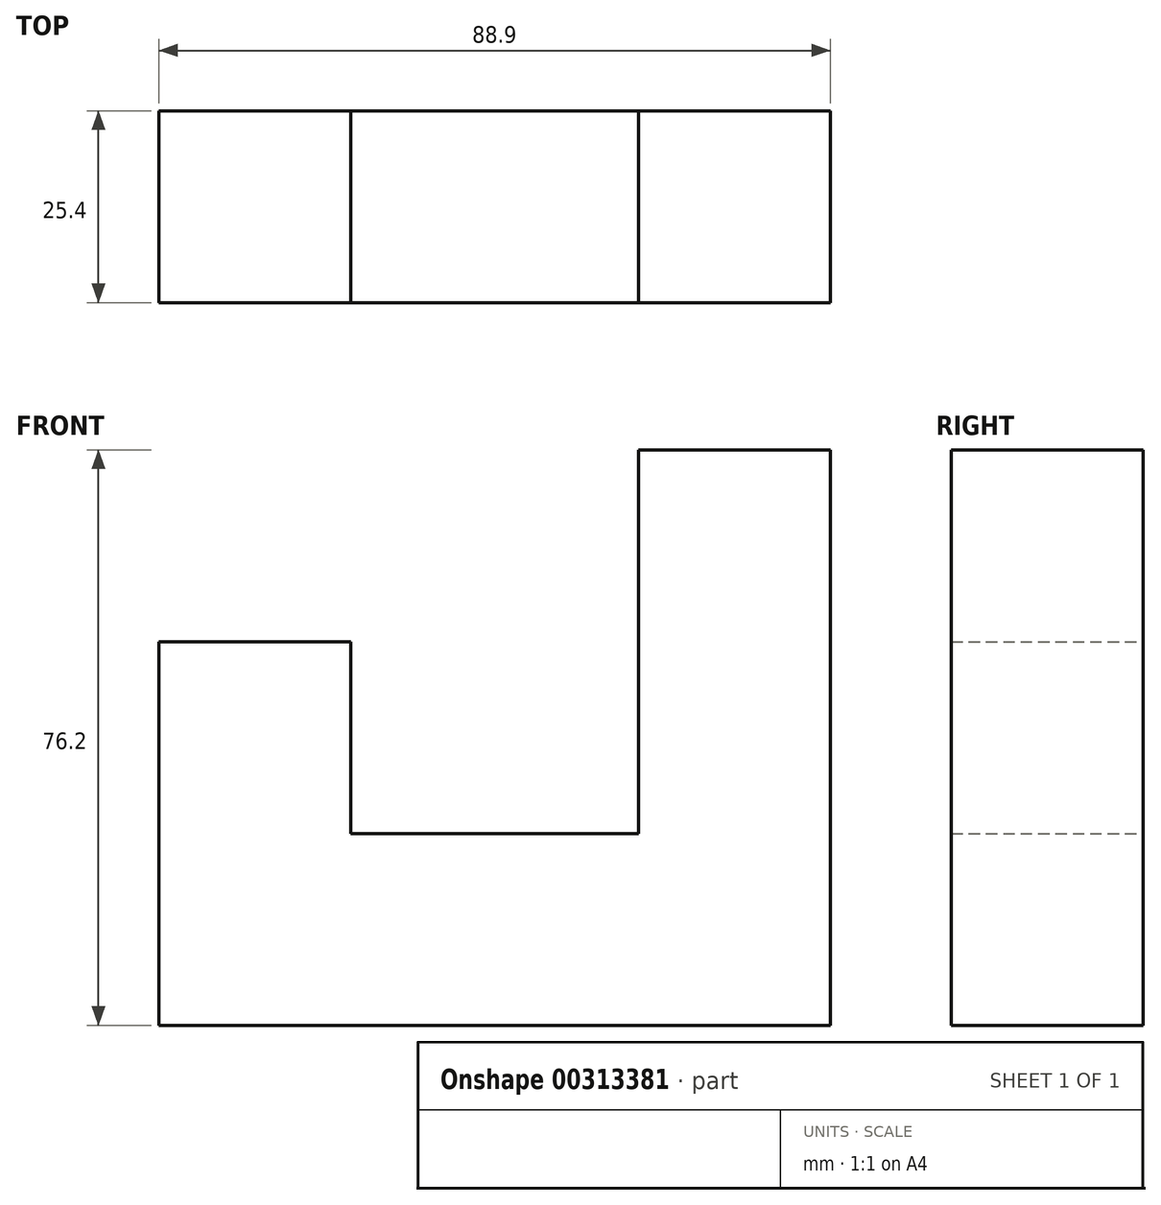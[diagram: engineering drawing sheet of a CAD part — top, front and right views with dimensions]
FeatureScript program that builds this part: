
annotation { "Feature Type Name" : "Feature", "Feature Type Description" : "" }
export const myFeature = defineFeature(function(context is Context, id is Id, definition is map)
    precondition{}
    {
        {
            var Q0;
            Q0=qCreatedBy(makeId("Front.planeOp"),FACE);
            var sketch = newSketch(context, id + "F0", { "sketchPlane" : qUnion([Q0])});
            skLineSegment(sketch, "E0", {"start": v(-43.6, -19.4) * mm, "end": v(45.3, -19.4) * mm});
            skLineSegment(sketch, "E1", {"start": v(45.3, -19.4) * mm, "end": v(45.3, 56.8) * mm});
            skLineSegment(sketch, "E2", {"start": v(45.3, 56.8) * mm, "end": v(19.9, 56.8) * mm});
            skLineSegment(sketch, "E3", {"start": v(19.9, 56.8) * mm, "end": v(19.9, 6) * mm});
            skLineSegment(sketch, "E4", {"start": v(19.9, 6) * mm, "end": v(-18.2, 6) * mm});
            skLineSegment(sketch, "E5", {"start": v(-18.2, 6) * mm, "end": v(-18.2, 31.4) * mm});
            skLineSegment(sketch, "E6", {"start": v(-18.2, 31.4) * mm, "end": v(-43.6, 31.4) * mm});
            skLineSegment(sketch, "E7", {"start": v(-43.6, 31.4) * mm, "end": v(-43.6, -19.4) * mm});
            skSolve(sketch);
        }
        {
            var Q0;
            Q0 = qSketchRegion(id + "F0", true);
            extrude(context, id + "F1", {"entities" : qUnion([Q0]), "depth" : 25.4 * mm});
        }
    });
